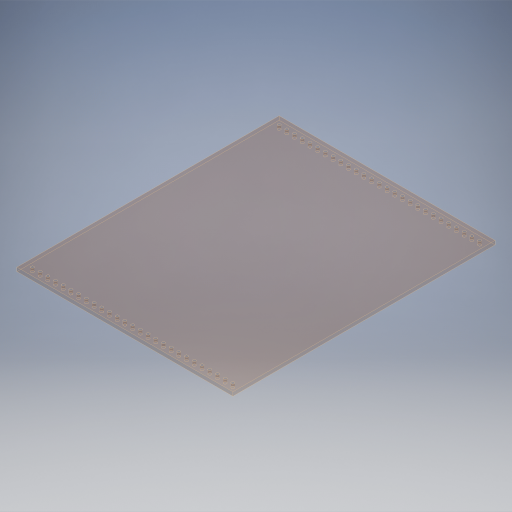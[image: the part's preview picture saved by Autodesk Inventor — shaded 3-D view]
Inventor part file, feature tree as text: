
AUTODESK INVENTOR PART (.ipt)
format: ipt  version: 2024.2 (Build 282272000, 272)  size: 359,936 bytes
history: native  units: in
note: dims shown in document units (in); Inventor stores cm internally (conversion verified against a paired STEP export)
features: extrude x1, sketch x1
ambient origin geometry x8: Origin, YZ Plane, XZ Plane, XY Plane, X Axis, Y Axis, Z Axis, Center Point
bodies: Body1 (feature_tree)
feature tree (2):
  extrude  "Extrusion4"  Depth=17.0in
  sketch  "Sketch4"  dims[d18=14.0in d19=17.0in d20=0.196in d21=0.5in d22=0.5in d23=10.6299in d25=0.5in d26=0.7874in d28=16.0in d31=0.25in d32=0.0in]
